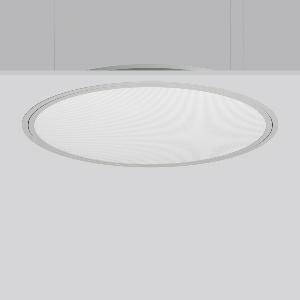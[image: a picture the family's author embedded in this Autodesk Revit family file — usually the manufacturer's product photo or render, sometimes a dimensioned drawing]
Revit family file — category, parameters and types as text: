
# Revit family: triona_round_e_312299_004_1_12_2303
name_source: partatom
category: Lighting Fixtures
units: mm (PartAtom-declared; Revit-internal decimal feet)

## family parameters
Cut with Voids When Loaded = No
Host = Face
Light Source = No
Part Type = Normal
Room Calculation Point = No
Round Connector Dimension = Use Diameter
Shared = No

## types (1)
- TRIONA round E (1 x LED Modul 840, 8350 lm, 4000)
    Apparent Load = 66 VA
    CIE Flux Codes = 59 87 97 100 100
    Color Rendering = 80
    Color Temperature = 4000
    Default Elevation = 1800 mm
    Description = Series: TRIONA round
Decorative round LED recessed surface luminaire. Cover made of sheet steel, powder-coated. Frame made of aluminium, powder-coated. Recessed ring: aluminium extrusion profile, powder coated. Light emission through a diffuser in plastic, opal/prismatic. Lightguide and diffuser made of non-yellowing plastic (PMMA). Lateral light emission (RZB SIDELITE technology) for above-average homogeneous light distribution. Suitable for installation in cavity ceilings. Tool-free mounting system thanks to the rocker arm mechanism (patent pending). Electronic ballast included. Very easy installation thanks to Plug+Play connection. 
Colour: silver, matt (approx. RAL 9006)
Diameter: 889 mm
Height: 2 mm
Cut-out diameter: 866 mm
Recess height: 100 mm
Luminaire: recess height: 89 mm
Lamp: LED
Socket: without socket
Colour temperature: 4000K
Colour rendering index (CRI): 80
System power: 66 W
Rated luminous flux: 8350 lm
Luminous efficiency: 127 lm/W
Control gear: Converter, dimmable, DALI
Protection class: I
Type of protection: IP 40
    Height = 0 mm  [stored 0 ft]
    Lamp = 1 x LED Modul 840
    Lamp Light Flux = 8350 lm
    Lamp count = 1
    Length = 889 mm
    Lifetime = 50000 h
    Luminous efficacy = 127 lm/W
    Manufacturer = RZB
    ModVariant = No
    Model = 312299.004.1.12
    Mounting Place = Ceiling
    Mounting Type = Recessed
    Number of Poles = 1
    OnlyDefault = Yes
    Power Factor = 1
    Product Name = TRIONA round E
    Product group = Recessed modular luminaires
    ProductGroupID = 406
    Protection Class = Protection class I
    Protection Degree = IP 20
    RLX_Detail_Level = 1
    RLX_Emergency_Light_Flux = 0 lm
    RLX_Emergency_Type = 0
    RLX_Emergency_Type_DB = No
    RlxData = <blob elided: 42037 chars, md5=a257d012>
    Socket = socket
    Standby Power = 0 W
    System Light Flux = 8350 lm
    System Power = 66 W
    Type Comments = Product without accessories
    Type Image = 312299.004.12.jpg
    URL = http://relux.com
    VarID = ---
    Voltage = 230 V
    Voltage Range = 220-240 V
    Weight = 0.00 kg
    Width = 0 mm  [stored 0 ft]

note: [stored X ft] marks values corroborated as IEEE doubles in the binary element streams (Revit-internal decimal feet)

## geometry (parser evidence)
native form markers: Blend x4, Sweep x10
no freeform markers — native parametric forms only
